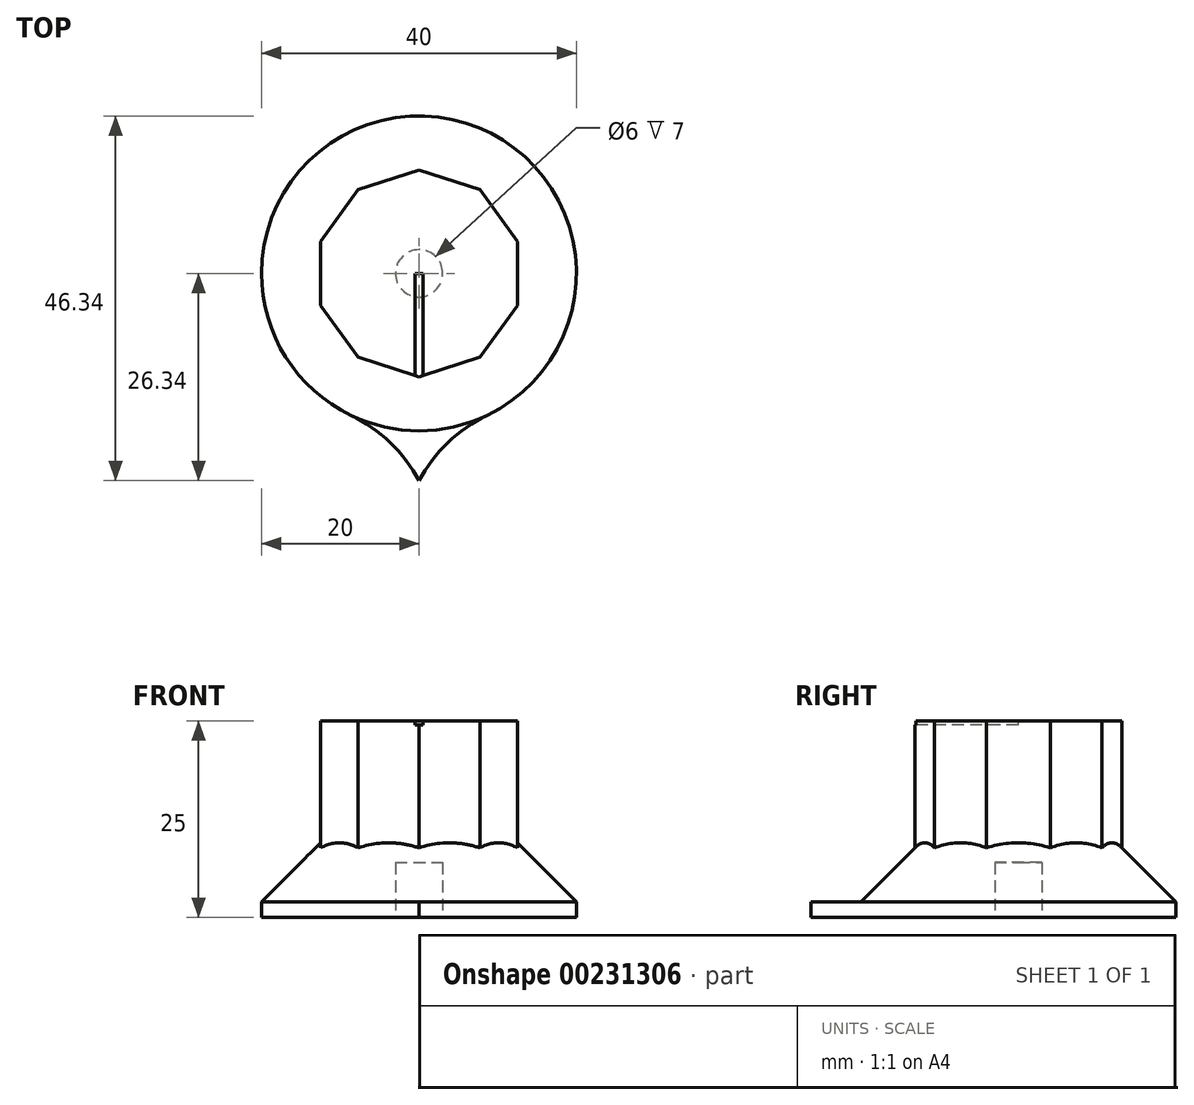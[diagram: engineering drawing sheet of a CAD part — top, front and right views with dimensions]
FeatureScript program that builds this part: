
annotation { "Feature Type Name" : "Feature", "Feature Type Description" : "" }
export const myFeature = defineFeature(function(context is Context, id is Id, definition is map)
    precondition{}
    {
        {
            var Q0;
            Q0=qCreatedBy(makeId("Top.planeOp"),FACE);
            var sketch = newSketch(context, id + "F0", { "sketchPlane" : qUnion([Q0])});
            skCircle(sketch, "E0.cCircle", {"center": v(0, 0) * mm, "radius": 12.5 * mm, "construction": true});
            skLineSegment(sketch, "E0.0", {"start": v(12.5, 4.06) * mm, "end": v(12.5, -4.06) * mm});
            skLineSegment(sketch, "E0.1", {"start": v(12.5, -4.06) * mm, "end": v(7.73, -10.63) * mm});
            skLineSegment(sketch, "E0.2", {"start": v(7.73, -10.63) * mm, "end": v(0, -13.14) * mm});
            skLineSegment(sketch, "E0.3", {"start": v(0, -13.14) * mm, "end": v(-7.73, -10.63) * mm});
            skLineSegment(sketch, "E0.4", {"start": v(-7.73, -10.63) * mm, "end": v(-12.5, -4.06) * mm});
            skLineSegment(sketch, "E0.5", {"start": v(-12.5, -4.06) * mm, "end": v(-12.5, 4.06) * mm});
            skLineSegment(sketch, "E0.6", {"start": v(-12.5, 4.06) * mm, "end": v(-7.73, 10.63) * mm});
            skLineSegment(sketch, "E0.7", {"start": v(-7.73, 10.63) * mm, "end": v(0, 13.14) * mm});
            skLineSegment(sketch, "E0.8", {"start": v(0, 13.14) * mm, "end": v(7.73, 10.63) * mm});
            skLineSegment(sketch, "E0.9", {"start": v(7.73, 10.63) * mm, "end": v(12.5, 4.06) * mm});
            skPoint(sketch, "E0.0.midPoint", {"position": v(12.5, 0) * mm});
            skSolve(sketch);
        }
        {
            var Q0;
            Q0 = qSketchRegion(id + "F0", true);
            extrude(context, id + "F1", {"entities" : qUnion([Q0]), "depth" : 25 * mm});
        }
        {
            var Q0;
            Q0=makeQuery(id+"F1.opExtrude","CAP_FACE",FACE,{"disambiguationData":[OSD([sQuery(id+"F0.wireOp",EDGE,"E0.0"),sQuery(id+"F0.wireOp",EDGE,"E0.1"),sQuery(id+"F0.wireOp",EDGE,"E0.2"),sQuery(id+"F0.wireOp",EDGE,"E0.3"),sQuery(id+"F0.wireOp",EDGE,"E0.4"),sQuery(id+"F0.wireOp",EDGE,"E0.5"),sQuery(id+"F0.wireOp",EDGE,"E0.6"),sQuery(id+"F0.wireOp",EDGE,"E0.7"),sQuery(id+"F0.wireOp",EDGE,"E0.8"),sQuery(id+"F0.wireOp",EDGE,"E0.9")])],"isStart":true});
            var sketch = newSketch(context, id + "F2", { "sketchPlane" : qUnion([Q0])});
            skCircle(sketch, "E1", {"center": v(0, 0) * mm, "radius": 20 * mm});
            skSolve(sketch);
        }
        {
            var Q0;
            Q0 = qSketchRegion(id + "F2", true);
            extrude(context, id + "F3", {"entities" : qUnion([Q0]), "operationType" : NewBodyOperationType.ADD, "oppositeDirection" : true, "depth" : 20 * mm});
        }
        {
            var Q0;
            Q0=makeQuery(id+"F3.opExtrude","CAP_EDGE",EDGE,{"disambiguationData":[OSD([sQuery(id+"F2.wireOp",EDGE,"E1")])],"isStart":false});
            chamfer(context, id + "F4", {"entities" : qUnion([Q0]), "width" : 18 * mm, "tangentPropagation" : true});
        }
        {
            var Q0;
            Q0=makeQuery(id+"F3.boolean.opBoolean","MERGE",FACE,{"derivedFrom":[makeQuery(id+"F1.opExtrude","CAP_FACE",FACE,{"disambiguationData":[OSD([sQuery(id+"F0.wireOp",EDGE,"E0.0"),sQuery(id+"F0.wireOp",EDGE,"E0.1"),sQuery(id+"F0.wireOp",EDGE,"E0.2"),sQuery(id+"F0.wireOp",EDGE,"E0.3"),sQuery(id+"F0.wireOp",EDGE,"E0.4"),sQuery(id+"F0.wireOp",EDGE,"E0.5"),sQuery(id+"F0.wireOp",EDGE,"E0.6"),sQuery(id+"F0.wireOp",EDGE,"E0.7"),sQuery(id+"F0.wireOp",EDGE,"E0.8"),sQuery(id+"F0.wireOp",EDGE,"E0.9")])],"isStart":true}),makeQuery(id+"F3.opExtrude","CAP_FACE",FACE,{"disambiguationData":[OSD([sQuery(id+"F2.wireOp",EDGE,"E1")])],"isStart":true})]});
            var sketch = newSketch(context, id + "F5", { "sketchPlane" : qUnion([Q0])});
            skLineSegment(sketch, "E2", {"start": v(0, 0) * mm, "end": v(0, 26.34) * mm, "construction": true});
            skArc(sketch, "E3", {"start": v(-8.64, 18.04) * mm, "mid": v(-3.66, 21.5) * mm, "end": v(0, 26.34) * mm});
            skArc(sketch, "E4.MirrorCS", {"start": v(8.64, 18.04) * mm, "mid": v(3.66, 21.5) * mm, "end": v(0, 26.34) * mm});
            skSolve(sketch);
        }
        {
            var Q0;
            {var subQ0=sQuery(id+"F5.wireOp",EDGE,"E3");Q0=makeQuery(id+"F5.imprint","IMPRINT",FACE,{"disambiguationData":[TD([[makeQuery(id+"F5.imprint","IMPRINT",EDGE,{"derivedFrom":subQ0}),-1.0]])]});}
            extrude(context, id + "F6", {"entities" : qUnion([Q0]), "operationType" : NewBodyOperationType.ADD, "oppositeDirection" : true, "depth" : 2 * mm});
        }
        {
            var Q0;
            {var subQ0=sQuery(id+"F2.wireOp",EDGE,"E1");Q0=makeQuery(id+"F6.boolean.opBoolean","MERGE",FACE,{"derivedFrom":[makeQuery(id+"F3.boolean.opBoolean","MERGE",FACE,{"derivedFrom":[makeQuery(id+"F1.opExtrude","CAP_FACE",FACE,{"disambiguationData":[OSD([sQuery(id+"F0.wireOp",EDGE,"E0.0"),sQuery(id+"F0.wireOp",EDGE,"E0.1"),sQuery(id+"F0.wireOp",EDGE,"E0.2"),sQuery(id+"F0.wireOp",EDGE,"E0.3"),sQuery(id+"F0.wireOp",EDGE,"E0.4"),sQuery(id+"F0.wireOp",EDGE,"E0.5"),sQuery(id+"F0.wireOp",EDGE,"E0.6"),sQuery(id+"F0.wireOp",EDGE,"E0.7"),sQuery(id+"F0.wireOp",EDGE,"E0.8"),sQuery(id+"F0.wireOp",EDGE,"E0.9")])],"isStart":true}),makeQuery(id+"F3.opExtrude","CAP_FACE",FACE,{"disambiguationData":[OSD([subQ0])],"isStart":true})]}),makeQuery(id+"F6.opExtrude","CAP_FACE",FACE,{"disambiguationData":[OSD([subQ0,sQuery(id+"F5.wireOp",EDGE,"E3"),sQuery(id+"F5.wireOp",EDGE,"E4.MirrorCS")])],"isStart":true})]});}
            var sketch = newSketch(context, id + "F7", { "sketchPlane" : qUnion([Q0])});
            skCircle(sketch, "E5", {"center": v(0, 0) * mm, "radius": 3 * mm});
            skSolve(sketch);
        }
        {
            var Q0;
            Q0 = qSketchRegion(id + "F7", true);
            extrude(context, id + "F8", {"entities" : qUnion([Q0]), "operationType" : NewBodyOperationType.REMOVE, "oppositeDirection" : true, "depth" : 7 * mm});
        }
        {
            var Q0;
            Q0=makeQuery(id+"F1.opExtrude","CAP_FACE",FACE,{"disambiguationData":[OSD([sQuery(id+"F0.wireOp",EDGE,"E0.0"),sQuery(id+"F0.wireOp",EDGE,"E0.1"),sQuery(id+"F0.wireOp",EDGE,"E0.2"),sQuery(id+"F0.wireOp",EDGE,"E0.3"),sQuery(id+"F0.wireOp",EDGE,"E0.4"),sQuery(id+"F0.wireOp",EDGE,"E0.5"),sQuery(id+"F0.wireOp",EDGE,"E0.6"),sQuery(id+"F0.wireOp",EDGE,"E0.7"),sQuery(id+"F0.wireOp",EDGE,"E0.8"),sQuery(id+"F0.wireOp",EDGE,"E0.9")])],"isStart":false});
            var sketch = newSketch(context, id + "F9", { "sketchPlane" : qUnion([Q0])});
            skLineSegment(sketch, "E6.bottom", {"start": v(-0.5, 0) * mm, "end": v(0.5, 0) * mm});
            skLineSegment(sketch, "E6.top", {"start": v(-0.5, -16.38) * mm, "end": v(0.5, -16.38) * mm});
            skLineSegment(sketch, "E6.left", {"start": v(-0.5, 0) * mm, "end": v(-0.5, -16.38) * mm});
            skLineSegment(sketch, "E6.right", {"start": v(0.5, 0) * mm, "end": v(0.5, -16.38) * mm});
            skSolve(sketch);
        }
        {
            var Q0;
            Q0 = qSketchRegion(id + "F9", true);
            extrude(context, id + "F10", {"entities" : qUnion([Q0]), "operationType" : NewBodyOperationType.REMOVE, "oppositeDirection" : true, "depth" : .5 * mm});
        }
    });
